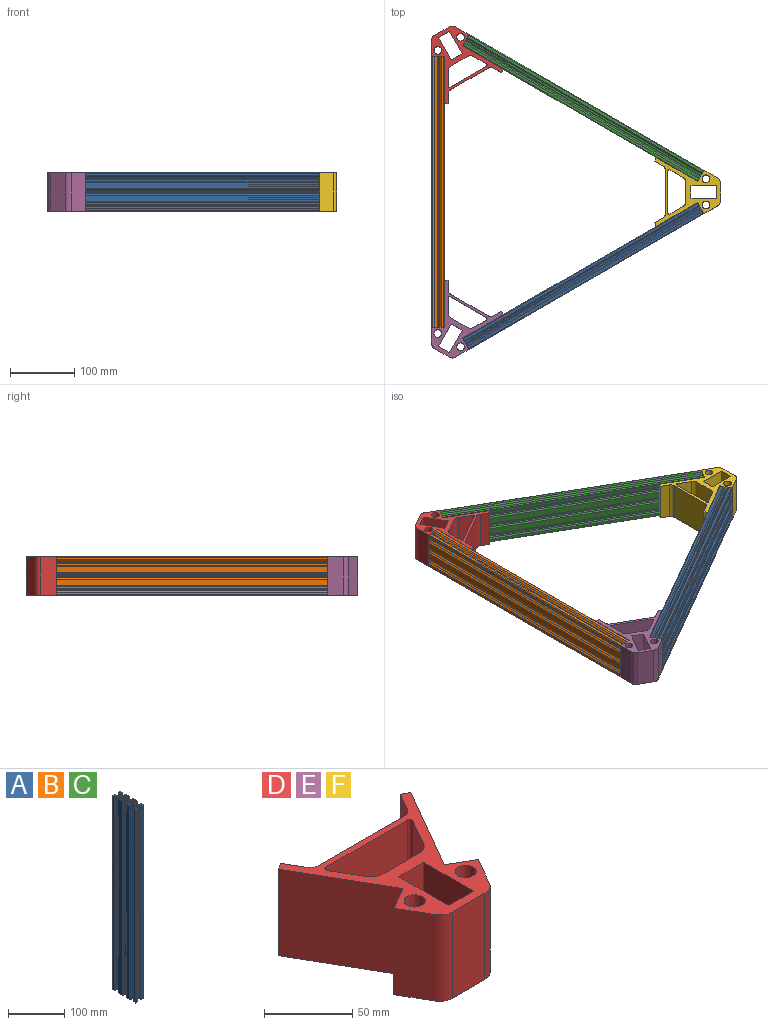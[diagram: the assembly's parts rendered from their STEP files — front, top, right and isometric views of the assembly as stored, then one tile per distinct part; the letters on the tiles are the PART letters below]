
ASSEMBLY  parts=6 mates=13
PART A: 141 faces, bbox 20x60x421 mm
  f0: plane 421x0.94mm, normal (0,1,0), area 395.5mm2, adj f1,f138,f139,f140
  f1: plane 421x3.06mm, normal (0.71,0.71,0), area 1822.3mm2, adj f0,f2,f139,f140
  f2: plane 421x2.42mm, normal (1,0,0), area 1018.7mm2, adj f1,f3,f139,f140
  f3: plane 421x0.52mm, normal (0.87,0.5,0), area 252.6mm2, adj f2,f4,f139,f140
  f4: plane 421x0.52mm, normal (0.87,-0.5,0), area 252.6mm2, adj f3,f5,f139,f140
  f5: plane 421x2.42mm, normal (1,0,0), area 1018.7mm2, adj f4,f6,f139,f140
  f6: plane 421x3.06mm, normal (0.71,-0.71,0), area 1822.3mm2, adj f5,f7,f139,f140
  f7: plane 421x0.94mm, normal (0,-1,0), area 395.5mm2, adj f6,f8,f139,f140
  f8: plane 421x3mm, normal (-1,0,0), area 1263mm2, adj f7,f9,f139,f140
  f9: plane 421x2mm, normal (0.71,-0.71,0), area 1190.8mm2, adj f8,f10,f139,f140
  f10: plane 421x4mm, normal (1,0,0), area 1684mm2, adj f9,f11,f139,f140
  f11: cylinder r=1mm len=421mm, axis (0,0,-1), area 661.3mm2, adj f10,f12,f139,f140
  f12: plane 421x4mm, normal (0,1,0), area 1684mm2, adj f11,f13,f139,f140
  f13: plane 421x2mm, normal (-0.71,0.71,0), area 1190.8mm2, adj f12,f14,f139,f140
  f14: plane 421x3mm, normal (0,-1,0), area 1263mm2, adj f13,f15,f139,f140
  f15: plane 421x0.94mm, normal (-1,0,0), area 395.5mm2, adj f14,f16,f139,f140
  f16: plane 421x3.06mm, normal (-0.71,0.71,0), area 1822.3mm2, adj f15,f17,f139,f140
  f17: plane 421x2.42mm, normal (0,1,0), area 1018.7mm2, adj f16,f18,f139,f140
  f18: plane 421x0.52mm, normal (-0.5,0.87,0), area 252.6mm2, adj f17,f19,f139,f140
  f19: plane 421x0.52mm, normal (0.5,0.87,0), area 252.6mm2, adj f18,f20,f139,f140
  f20: plane 421x2.42mm, normal (0,1,0), area 1018.7mm2, adj f19,f21,f139,f140
  f21: plane 421x3.06mm, normal (0.71,0.71,0), area 1822.3mm2, adj f20,f22,f139,f140
  f22: plane 421x0.94mm, normal (1,0,0), area 395.5mm2, adj f21,f23,f139,f140
  f23: plane 421x3mm, normal (0,-1,0), area 1263mm2, adj f22,f24,f139,f140
  f24: plane 421x2mm, normal (0.71,0.71,0), area 1190.8mm2, adj f23,f25,f139,f140
  f25: plane 421x4mm, normal (0,1,0), area 1684mm2, adj f24,f26,f139,f140
  f26: cylinder r=1mm len=421mm, axis (0,0,-1), area 661.3mm2, adj f25,f27,f139,f140
  f27: plane 421x4mm, normal (-1,0,0), area 1684mm2, adj f26,f28,f139,f140
  f28: plane 421x2mm, normal (-0.71,-0.71,0), area 1190.8mm2, adj f27,f29,f139,f140
  f29: plane 421x3mm, normal (1,0,0), area 1263mm2, adj f28,f30,f139,f140
  f30: plane 421x0.94mm, normal (0,-1,0), area 395.5mm2, adj f29,f31,f139,f140
  f31: plane 421x3.06mm, normal (-0.71,-0.71,0), area 1822.3mm2, adj f30,f32,f139,f140
  f32: plane 421x2.42mm, normal (-1,0,0), area 1018.7mm2, adj f31,f33,f139,f140
  f33: plane 421x0.52mm, normal (-0.87,-0.5,0), area 252.6mm2, adj f32,f34,f139,f140
  f34: plane 421x0.52mm, normal (-0.87,0.5,0), area 252.6mm2, adj f33,f35,f139,f140
  f35: plane 421x2.42mm, normal (-1,0,0), area 1018.7mm2, adj f34,f36,f139,f140
  f36: plane 421x3.06mm, normal (-0.71,0.71,0), area 1822.3mm2, adj f35,f37,f139,f140
  f37: plane 421x0.94mm, normal (0,1,0), area 395.5mm2, adj f36,f38,f139,f140
  f38: plane 421x3mm, normal (1,0,0), area 1263mm2, adj f37,f39,f139,f140
  f39: plane 421x2mm, normal (-0.71,0.71,0), area 1190.8mm2, adj f38,f40,f139,f140
  f40: plane 421x10mm, normal (-1,0,0), area 4210mm2, adj f39,f41,f139,f140
  f41: plane 421x2mm, normal (-0.71,-0.71,0), area 1190.8mm2, adj f40,f42,f139,f140
  f42: plane 421x3mm, normal (1,0,0), area 1263mm2, adj f41,f43,f139,f140
  f43: plane 421x0.94mm, normal (0,-1,0), area 395.5mm2, adj f42,f44,f139,f140
  f44: plane 421x3.06mm, normal (-0.71,-0.71,0), area 1822.3mm2, adj f43,f45,f139,f140
  f45: plane 421x2.42mm, normal (-1,0,0), area 1018.7mm2, adj f44,f46,f139,f140
  f46: plane 421x0.52mm, normal (-0.87,-0.5,0), area 252.6mm2, adj f45,f47,f139,f140
  f47: plane 421x0.52mm, normal (-0.87,0.5,0), area 252.6mm2, adj f46,f48,f139,f140
  f48: plane 421x2.42mm, normal (-1,0,0), area 1018.7mm2, adj f47,f49,f139,f140
  f49: plane 421x3.06mm, normal (-0.71,0.71,0), area 1822.3mm2, adj f48,f50,f139,f140
  f50: plane 421x0.94mm, normal (0,1,0), area 395.5mm2, adj f49,f51,f139,f140
  f51: plane 421x3mm, normal (1,0,0), area 1263mm2, adj f50,f52,f139,f140
  f52: plane 421x2mm, normal (-0.71,0.71,0), area 1190.8mm2, adj f51,f53,f139,f140
  f53: plane 421x10mm, normal (-1,0,0), area 4210mm2, adj f52,f54,f139,f140
  f54: plane 421x2mm, normal (-0.71,-0.71,0), area 1190.8mm2, adj f53,f55,f139,f140
  f55: plane 421x3mm, normal (1,0,0), area 1263mm2, adj f54,f56,f139,f140
  f56: plane 421x0.94mm, normal (0,-1,0), area 395.5mm2, adj f55,f57,f139,f140
  f57: plane 421x3.06mm, normal (-0.71,-0.71,0), area 1822.3mm2, adj f56,f58,f139,f140
  f58: plane 421x2.42mm, normal (-1,0,0), area 1018.7mm2, adj f57,f59,f139,f140
  f59: plane 421x0.52mm, normal (-0.87,-0.5,0), area 252.6mm2, adj f58,f60,f139,f140
  f60: plane 421x0.52mm, normal (-0.87,0.5,0), area 252.6mm2, adj f59,f61,f139,f140
  f61: plane 421x2.42mm, normal (-1,0,0), area 1018.7mm2, adj f60,f62,f139,f140
  f62: plane 421x3.06mm, normal (-0.71,0.71,0), area 1822.3mm2, adj f61,f63,f139,f140
  f63: plane 421x0.94mm, normal (0,1,0), area 395.5mm2, adj f62,f64,f139,f140
  f64: plane 421x3mm, normal (1,0,0), area 1263mm2, adj f63,f65,f139,f140
  f65: plane 421x2mm, normal (-0.71,0.71,0), area 1190.8mm2, adj f64,f66,f139,f140
  f66: plane 421x4mm, normal (-1,0,0), area 1684mm2, adj f65,f67,f139,f140
  f67: cylinder r=1mm len=421mm, axis (0,0,-1), area 661.3mm2, adj f66,f68,f139,f140
  f68: plane 421x4mm, normal (0,-1,0), area 1684mm2, adj f67,f69,f139,f140
  f69: plane 421x2mm, normal (0.71,-0.71,0), area 1190.8mm2, adj f68,f70,f139,f140
  f70: plane 421x3mm, normal (0,1,0), area 1263mm2, adj f69,f71,f139,f140
  f71: plane 421x0.94mm, normal (1,0,0), area 395.5mm2, adj f70,f72,f139,f140
  f72: plane 421x3.06mm, normal (0.71,-0.71,0), area 1822.3mm2, adj f71,f73,f139,f140
  f73: plane 421x2.42mm, normal (0,-1,0), area 1018.7mm2, adj f72,f74,f139,f140
  f74: plane 421x0.52mm, normal (0.5,-0.87,0), area 252.6mm2, adj f73,f75,f139,f140
  f75: plane 421x0.52mm, normal (-0.5,-0.87,0), area 252.6mm2, adj f74,f76,f139,f140
  f76: plane 421x2.42mm, normal (0,-1,0), area 1018.7mm2, adj f75,f77,f139,f140
  f77: plane 421x3.06mm, normal (-0.71,-0.71,0), area 1822.3mm2, adj f76,f78,f139,f140
  f78: plane 421x0.94mm, normal (-1,0,0), area 395.5mm2, adj f77,f79,f139,f140
  f79: plane 421x3mm, normal (0,1,0), area 1263mm2, adj f78,f80,f139,f140
  f80: plane 421x2mm, normal (-0.71,-0.71,0), area 1190.8mm2, adj f79,f81,f139,f140
  f81: plane 421x4mm, normal (0,-1,0), area 1684mm2, adj f80,f82,f139,f140
  f82: cylinder r=1mm len=421mm, axis (0,0,-1), area 661.3mm2, adj f81,f83,f139,f140
  f83: plane 421x4mm, normal (1,0,0), area 1684mm2, adj f82,f84,f139,f140
  f84: plane 421x2mm, normal (0.71,0.71,0), area 1190.8mm2, adj f83,f85,f139,f140
  f85: plane 421x3mm, normal (-1,0,0), area 1263mm2, adj f84,f86,f139,f140
  f86: plane 421x0.94mm, normal (0,1,0), area 395.5mm2, adj f85,f87,f139,f140
  f87: plane 421x3.06mm, normal (0.71,0.71,0), area 1822.3mm2, adj f86,f88,f139,f140
  f88: plane 421x2.42mm, normal (1,0,0), area 1018.7mm2, adj f87,f89,f139,f140
  f89: plane 421x0.52mm, normal (0.87,0.5,0), area 252.6mm2, adj f88,f90,f139,f140
  f90: plane 421x0.52mm, normal (0.87,-0.5,0), area 252.6mm2, adj f89,f91,f139,f140
  f91: plane 421x2.42mm, normal (1,0,0), area 1018.7mm2, adj f90,f92,f139,f140
  f92: plane 421x3.06mm, normal (0.71,-0.71,0), area 1822.3mm2, adj f91,f93,f139,f140
  f93: plane 421x0.94mm, normal (0,-1,0), area 395.5mm2, adj f92,f94,f139,f140
  f94: plane 421x3mm, normal (-1,0,0), area 1263mm2, adj f93,f95,f139,f140
  f95: plane 421x2mm, normal (0.71,-0.71,0), area 1190.8mm2, adj f94,f96,f139,f140
  f96: plane 421x10mm, normal (1,0,0), area 4210mm2, adj f95,f97,f139,f140
  f97: plane 421x2mm, normal (0.71,0.71,0), area 1190.8mm2, adj f96,f98,f139,f140
  f98: plane 421x3mm, normal (-1,0,0), area 1263mm2, adj f97,f99,f139,f140
  f99: plane 421x0.94mm, normal (0,1,0), area 395.5mm2, adj f98,f100,f139,f140
  f100: plane 421x3.06mm, normal (0.71,0.71,0), area 1822.3mm2, adj f99,f101,f139,f140
  f101: plane 421x2.42mm, normal (1,0,0), area 1018.7mm2, adj f100,f102,f139,f140
  f102: plane 421x0.52mm, normal (0.87,0.5,0), area 252.6mm2, adj f101,f103,f139,f140
  f103: plane 421x0.52mm, normal (0.87,-0.5,0), area 252.6mm2, adj f102,f104,f139,f140
  f104: plane 421x2.42mm, normal (1,0,0), area 1018.7mm2, adj f103,f105,f139,f140
  f105: plane 421x3.06mm, normal (0.71,-0.71,0), area 1822.3mm2, adj f104,f106,f139,f140
  f106: plane 421x0.94mm, normal (0,-1,0), area 395.5mm2, adj f105,f107,f139,f140
  f107: plane 421x3mm, normal (-1,0,0), area 1263mm2, adj f106,f108,f139,f140
  f108: plane 421x2mm, normal (0.71,-0.71,0), area 1190.8mm2, adj f107,f109,f139,f140
  f109: plane 421x10mm, normal (1,0,0), area 4210mm2, adj f108,f110,f139,f140
  f110: plane 421x2mm, normal (0.71,0.71,0), area 1190.8mm2, adj f109,f138,f139,f140
  f111: plane 421x1.06mm, normal (0,-1,0), area 446.5mm2, adj f112,f136,f139,f140
  f112: plane 421x4mm, normal (0.71,-0.71,0), area 2381.5mm2, adj f111,f113,f139,f140
  f113: plane 421x5.88mm, normal (0,-1,0), area 2474.9mm2, adj f112,f114,f139,f140
  f114: plane 421x4mm, normal (-0.71,-0.71,0), area 2381.5mm2, adj f113,f115,f139,f140
  f115: plane 421x1.06mm, normal (0,-1,0), area 446.5mm2, adj f114,f116,f139,f140
  f116: plane 421x4mm, normal (-1,0,0), area 1684mm2, adj f115,f117,f139,f140
  f117: plane 421x1.06mm, normal (0,1,0), area 446.5mm2, adj f116,f118,f139,f140
  f118: plane 421x4mm, normal (-0.71,0.71,0), area 2381.5mm2, adj f117,f119,f139,f140
  f119: plane 421x5.88mm, normal (0,1,0), area 2474.9mm2, adj f118,f120,f139,f140
  f120: plane 421x4mm, normal (0.71,0.71,0), area 2381.5mm2, adj f119,f121,f139,f140
  f121: plane 421x1.06mm, normal (0,1,0), area 446.5mm2, adj f120,f136,f139,f140
  f122: plane 421x4mm, normal (1,0,0), area 1684mm2, adj f123,f137,f139,f140
  f123: plane 421x1.06mm, normal (0,-1,0), area 446.5mm2, adj f122,f124,f139,f140
  f124: plane 421x4mm, normal (0.71,-0.71,0), area 2381.5mm2, adj f123,f125,f139,f140
  f125: plane 421x5.88mm, normal (0,-1,0), area 2474.9mm2, adj f124,f126,f139,f140
  f126: plane 421x4mm, normal (-0.71,-0.71,0), area 2381.5mm2, adj f125,f127,f139,f140
  f127: plane 421x1.06mm, normal (0,-1,0), area 446.5mm2, adj f126,f128,f139,f140
  f128: plane 421x4mm, normal (-1,0,0), area 1684mm2, adj f127,f129,f139,f140
  f129: plane 421x1.06mm, normal (0,1,0), area 446.5mm2, adj f128,f130,f139,f140
  f130: plane 421x4mm, normal (-0.71,0.71,0), area 2381.5mm2, adj f129,f131,f139,f140
  f131: plane 421x5.88mm, normal (0,1,0), area 2474.9mm2, adj f130,f132,f139,f140
  f132: plane 421x4mm, normal (0.71,0.71,0), area 2381.5mm2, adj f131,f137,f139,f140
  f133: cylinder r=2.1mm len=421mm, axis (0,0,-1), area 5555mm2, adj f139,f140
  f134: cylinder r=2.1mm len=421mm, axis (0,0,-1), area 5555mm2, adj f139,f140
  f135: cylinder r=2.1mm len=421mm, axis (0,0,-1), area 5555mm2, adj f139,f140
  f136: plane 421x4mm, normal (1,0,0), area 1684mm2, adj f111,f121,f139,f140
  f137: plane 421x1.06mm, normal (0,1,0), area 446.5mm2, adj f122,f132,f139,f140
  f138: plane 421x3mm, normal (-1,0,0), area 1263mm2, adj f0,f110,f139,f140
  f139: plane 60x20mm, normal (0,0,1), area 433.2mm2, adj f0,f1,f2,f3,f4,f5,f6,f7
  f140: plane 60x20mm, normal (0,0,-1), area 433.2mm2, adj f0,f1,f2,f3,f4,f5,f6,f7
PART B: same geometry as A
PART C: same geometry as A
PART D: 32 faces, bbox 106.4x102.5x60 mm
  f0: plane 60x21.01mm, normal (-0.87,-0.5,0), area 1455.3mm2, adj f1,f29,f30,f31
  f1: cylinder r=10mm len=60mm, axis (0,0,-1), area 628.3mm2, adj f0,f2,f30,f31
  f2: plane 60x26.14mm, normal (0,-1,0), area 1568.1mm2, adj f1,f3,f30,f31
  f3: cylinder r=10mm len=60mm, axis (0,0,-1), area 628.3mm2, adj f2,f4,f30,f31
  f4: plane 60x21.01mm, normal (0.87,-0.5,0), area 1455.3mm2, adj f3,f5,f30,f31
  f5: plane 60x17.32mm, normal (0.5,0.87,0), area 1200mm2, adj f4,f6,f30,f31
  f6: plane 63.51x60mm, normal (0.87,-0.5,0), area 4400.4mm2, adj f5,f7,f30,f31
  f7: plane 60x5.2mm, normal (0.5,0.87,0), area 360mm2, adj f6,f8,f30,f31
  f8: plane 60x12.77mm, normal (-0.87,0.5,0), area 884.7mm2, adj f7,f9,f30,f31
  f9: cylinder r=8mm len=60mm, axis (0,0,-1), area 502.7mm2, adj f8,f10,f30,f31
  f10: plane 67.42x60mm, normal (0,1,0), area 4044.9mm2, adj f9,f11,f30,f31
  f11: cylinder r=8mm len=60mm, axis (0,0,-1), area 502.7mm2, adj f10,f12,f30,f31
  f12: plane 60x12.77mm, normal (0.87,0.5,0), area 884.7mm2, adj f11,f13,f30,f31
  f13: plane 60x5.2mm, normal (-0.5,0.87,0), area 360mm2, adj f12,f14,f30,f31
  f14: plane 63.51x60mm, normal (-0.87,-0.5,0), area 4400.4mm2, adj f13,f29,f30,f31
  f15: cylinder r=10mm len=60mm, axis (0,0,-1), area 628.3mm2, adj f16,f27,f30,f31
  f16: plane 60x19.75mm, normal (0.87,0.5,0), area 1368.3mm2, adj f15,f17,f30,f31
  f17: cylinder r=2mm len=60mm, axis (0,0,-1), area 251.3mm2, adj f16,f18,f30,f31
  f18: plane 65.11x60mm, normal (0,-1,0), area 3906.4mm2, adj f17,f19,f30,f31
  f19: cylinder r=2mm len=60mm, axis (0,0,-1), area 251.3mm2, adj f18,f20,f30,f31
  f20: plane 60x19.75mm, normal (-0.87,0.5,0), area 1368.3mm2, adj f19,f21,f30,f31
  f21: cylinder r=10mm len=60mm, axis (0,0,-1), area 628.3mm2, adj f20,f27,f30,f31
  f22: plane 60x40mm, normal (-1,0,0), area 2400mm2, adj f23,f28,f30,f31
  f23: plane 60x20mm, normal (0,1,0), area 1200mm2, adj f22,f24,f30,f31
  f24: plane 60x40mm, normal (1,0,0), area 2400mm2, adj f23,f28,f30,f31
  f25: cylinder r=6mm len=60mm, axis (0,0,-1), area 2261.9mm2, adj f30,f31
  f26: cylinder r=6mm len=60mm, axis (0,0,-1), area 2261.9mm2, adj f30,f31
  f27: plane 60x28.44mm, normal (0,1,0), area 1706.7mm2, adj f15,f21,f30,f31
  f28: plane 60x20mm, normal (0,-1,0), area 1200mm2, adj f22,f24,f30,f31
  f29: plane 60x17.32mm, normal (-0.5,0.87,0), area 1200mm2, adj f0,f14,f30,f31
  f30: plane 106.41x102.52mm, normal (0,0,1), area 2591.4mm2, adj f0,f1,f2,f3,f4,f5,f6,f7
  f31: plane 106.41x102.52mm, normal (0,0,-1), area 2591.4mm2, adj f0,f1,f2,f3,f4,f5,f6,f7
PART E: same geometry as D
PART F: same geometry as D
PLACE A rot(axis=(0.77,-0.45,-0.45),104.5deg) t=(274.12,-13.31,-20.89)mm
PLACE B rot(axis=(1,0,0),90deg) t=(-134.11,222.39,-20.89)mm
PLACE C rot(axis=(0.38,-0.65,-0.65),138.6deg) t=(274.12,37.08,-20.89)mm
PLACE D rot(axis=(0,0,-1),150deg) t=(-102.91,218.74,-50.89)mm
PLACE E rot(axis=(0,0,-1),30deg) t=(-102.91,-194.97,-50.89)mm
PLACE F rot(axis=(0,0,1),90deg) t=(255.37,11.89,-50.89)mm
MATE planar D.f30 <-> C.f12  axis (0,0,1) through (-96.13,227,9.11)mm
MATE planar A.f25 <-> F.f30  axis (0,0,1) through (88.33,-112.49,9.11)mm
MATE planar D.f14 <-> C.f96  axis (0.5,0.87,0) through (-63.71,220.59,-20.89)mm
MATE planar E.f30 <-> A.f25  axis (0,0,1) through (-55.73,-180.65,9.11)mm
MATE planar C.f12 <-> F.f30  axis (0,0,1) through (270.62,31.02,9.11)mm
MATE planar A.f133 <-> E.f5  axis (-0.87,-0.5,0) through (-90.47,-223.81,-20.89)mm
MATE planar F.f29 <-> A.f140  axis (-0.87,-0.5,0) through (274.12,-13.31,-20.89)mm
MATE planar F.f6 <-> C.f109  axis (0.5,0.87,0) through (237.37,46.76,-20.89)mm
MATE planar E.f6 <-> A.f40  axis (0.5,-0.87,0) through (-63.71,-196.81,-20.89)mm
MATE planar C.f140 <-> F.f5  axis (0.87,-0.5,0) through (274.12,37.08,-16.89)mm
MATE planar F.f14 <-> A.f53  axis (0.5,-0.87,0) through (237.37,-22.98,-20.89)mm
MATE fastened B.f133 <-> D.f5  axis (0,1,0) through (-134.11,222.39,-20.89)mm
MATE fastened C.f133 <-> D.f29  axis (-0.87,0.5,0) through (-90.47,247.58,-20.89)mm
